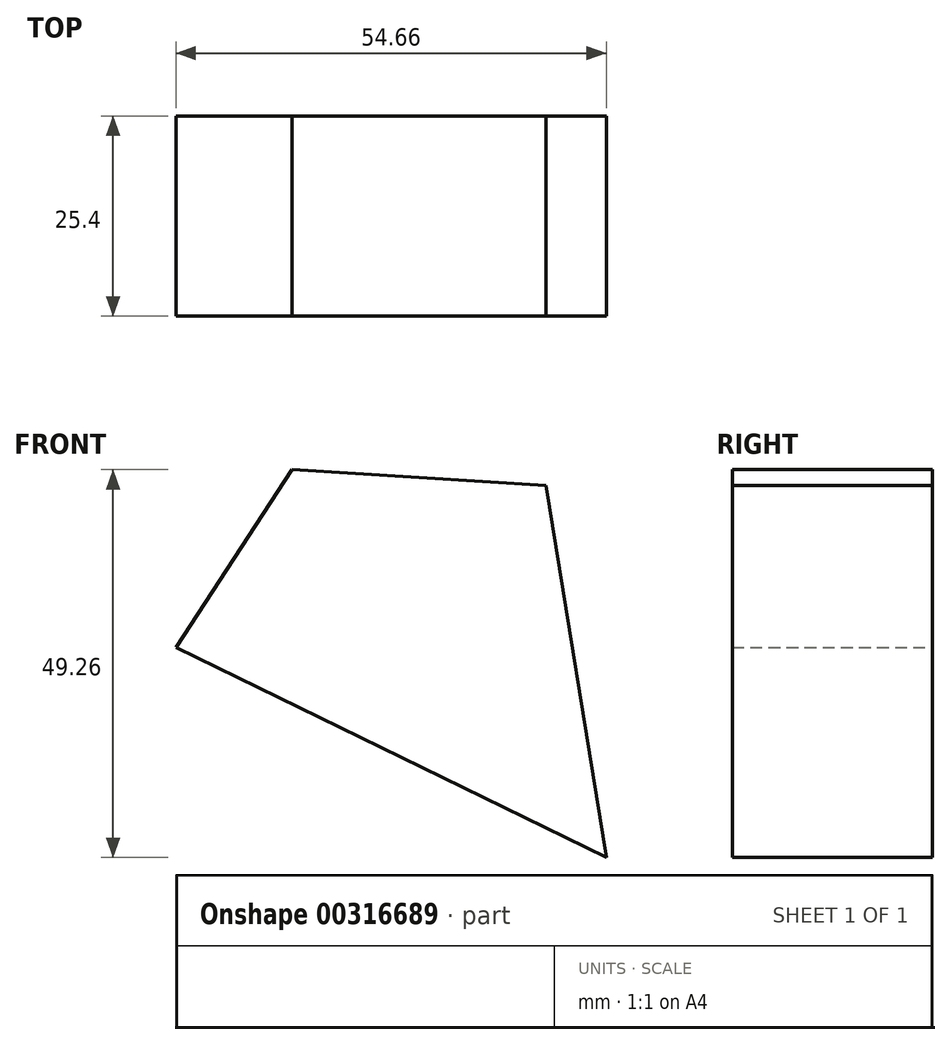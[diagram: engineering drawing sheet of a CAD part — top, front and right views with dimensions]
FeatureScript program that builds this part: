
annotation { "Feature Type Name" : "Feature", "Feature Type Description" : "" }
export const myFeature = defineFeature(function(context is Context, id is Id, definition is map)
    precondition{}
    {
        {
            var Q0;
            Q0=qCreatedBy(makeId("Front.planeOp"),FACE);
            var sketch = newSketch(context, id + "F0", { "sketchPlane" : qUnion([Q0])});
            skLineSegment(sketch, "E0", {"start": v(-54.66, 26.67) * mm, "end": v(-39.9, 49.26) * mm});
            skLineSegment(sketch, "E1", {"start": v(-39.9, 49.26) * mm, "end": v(-7.64, 47.26) * mm});
            skLineSegment(sketch, "E2", {"start": v(-7.64, 47.26) * mm, "end": v(0, 0) * mm});
            skLineSegment(sketch, "E3", {"start": v(0, 0) * mm, "end": v(-54.66, 26.67) * mm});
            skSolve(sketch);
        }
        {
            var Q0;
            Q0=makeQuery(id+"F0.imprint","IMPRINT",FACE,{"disambiguationData":[TD([[makeQuery(id+"F0.imprint","IMPRINT",EDGE,{"derivedFrom":sQuery(id+"F0.wireOp",EDGE,"E0")}),-1.0]])]});
            extrude(context, id + "F1", {"entities" : qUnion([Q0]), "depth" : 25.4 * mm});
        }
    });
